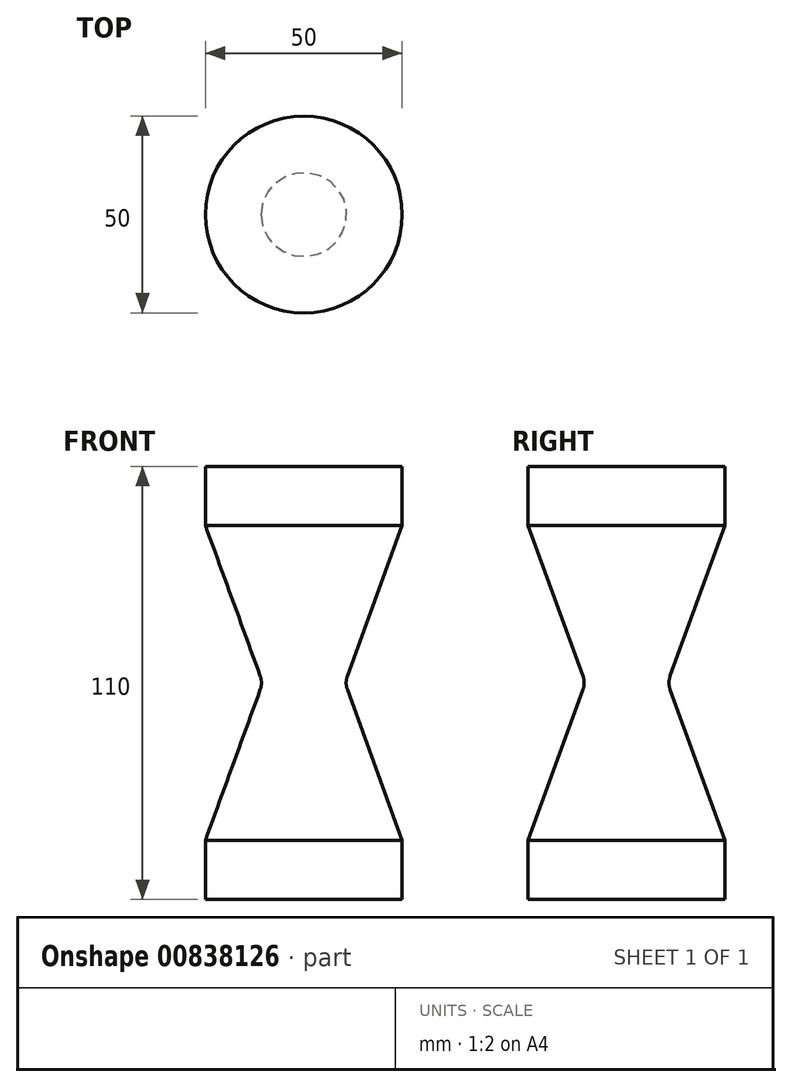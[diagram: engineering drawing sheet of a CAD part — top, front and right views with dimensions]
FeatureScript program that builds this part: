
annotation { "Feature Type Name" : "Feature", "Feature Type Description" : "" }
export const myFeature = defineFeature(function(context is Context, id is Id, definition is map)
    precondition{}
    {
        {
            var Q0;
            Q0=qCreatedBy(makeId("Front.planeOp"),FACE);
            var sketch = newSketch(context, id + "F0", { "sketchPlane" : qUnion([Q0])});
            skLineSegment(sketch, "E0", {"start": v(0, 0) * mm, "end": v(0, 110) * mm});
            skLineSegment(sketch, "E1", {"start": v(0, 0) * mm, "end": v(25, 0) * mm});
            skLineSegment(sketch, "E2", {"start": v(25, 0) * mm, "end": v(25, 15) * mm});
            skLineSegment(sketch, "E3", {"start": v(25, 15) * mm, "end": v(10.44, 55) * mm});
            skPoint(sketch, "E3.endSnap0", {"position": v(0, 55) * mm});
            skLineSegment(sketch, "E4", {"start": v(0, 55) * mm, "end": v(33.7, 55) * mm, "construction": true});
            skLineSegment(sketch, "E5.MirrorCS", {"start": v(25, 95) * mm, "end": v(10.44, 55) * mm});
            skLineSegment(sketch, "E6.MirrorCS", {"start": v(25, 110) * mm, "end": v(25, 95) * mm});
            skLineSegment(sketch, "E7.MirrorCS", {"start": v(0, 110) * mm, "end": v(25, 110) * mm});
            skSolve(sketch);
        }
        {
            var Q0;
            Q0 = qSketchRegion(id + "F0", true);
            var Q1;
            Q1=sQuery(id+"F0.wireOp",EDGE,"E0");
            revolve(context, id + "F1", {"surfaceOperationType" : NewSurfaceOperationType.NEW, "entities" : qUnion([Q0]), "axis" : qUnion([Q1]), "revolveType" : RevolveType.FULL});
        }
        {
            var Q0;
            Q0=makeQuery(id+"F1.opRevolve","SWEPT_EDGE",EDGE,{"disambiguationData":[OSD([sQuery(id+"F0.wireOp",EDGE,"E3"),sQuery(id+"F0.wireOp",EDGE,"E5.MirrorCS")])]});
            fillet(context, id + "F2", {"entities" : qUnion([Q0]), "radius" : 5 * mm, "tangentPropagation" : true, "allowEdgeOverflow" : false});
        }
    });
